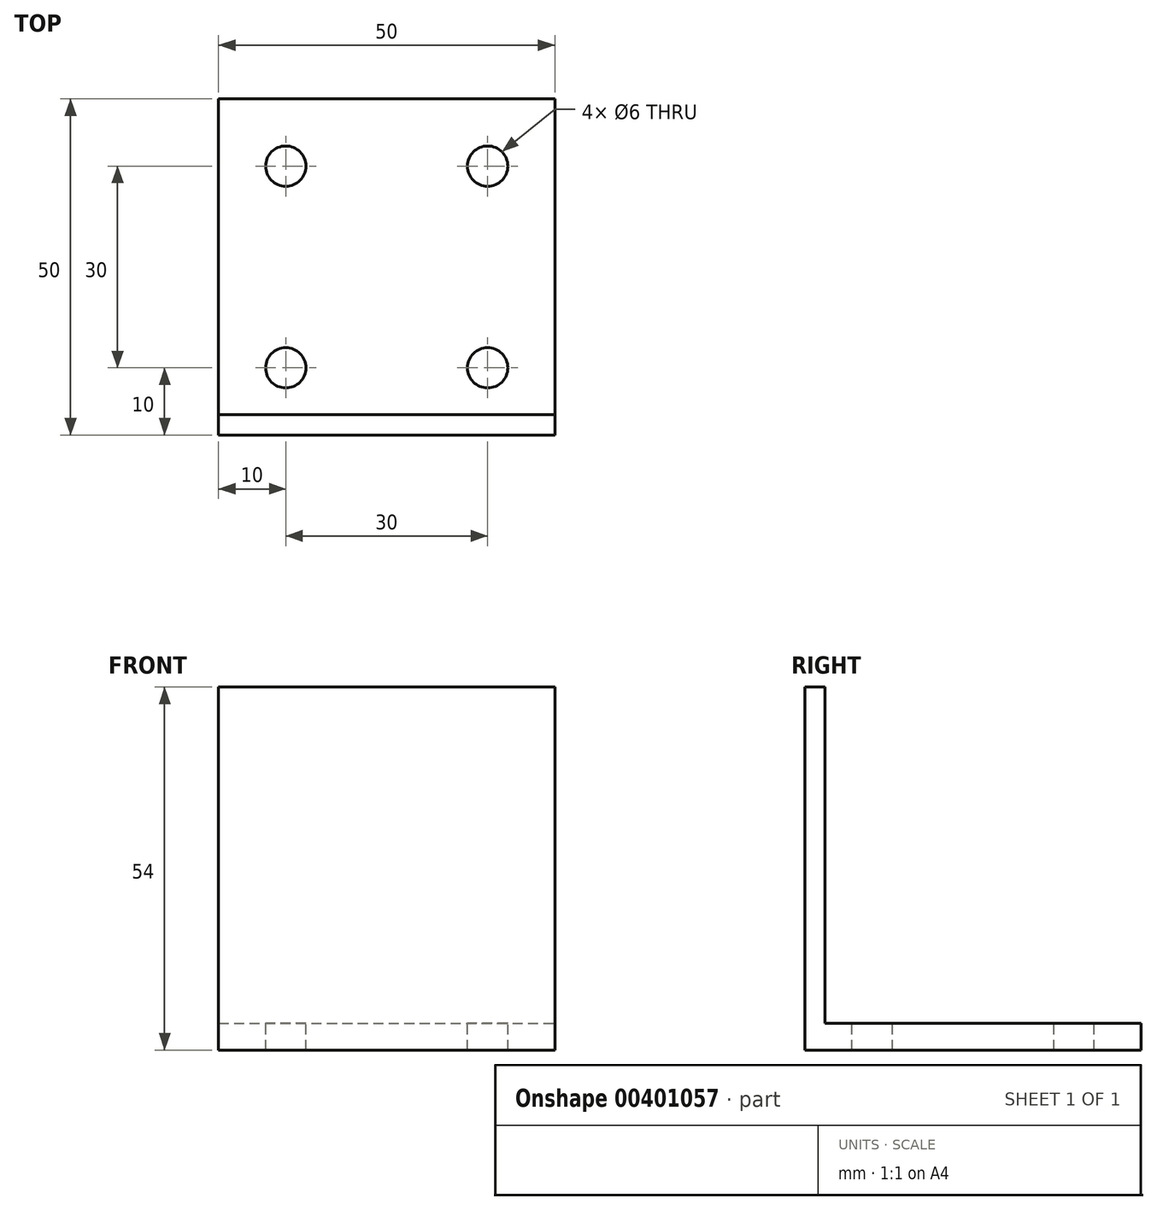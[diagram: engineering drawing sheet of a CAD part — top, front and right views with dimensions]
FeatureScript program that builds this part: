
annotation { "Feature Type Name" : "Feature", "Feature Type Description" : "" }
export const myFeature = defineFeature(function(context is Context, id is Id, definition is map)
    precondition{}
    {
        {
            var Q0;
            Q0=qCreatedBy(makeId("Top.planeOp"),FACE);
            var sketch = newSketch(context, id + "F0", { "sketchPlane" : qUnion([Q0])});
            skLineSegment(sketch, "E0.bottom", {"start": v(-25, 25) * mm, "end": v(25, 25) * mm});
            skLineSegment(sketch, "E0.top", {"start": v(-25, -25) * mm, "end": v(25, -25) * mm});
            skLineSegment(sketch, "E0.left", {"start": v(-25, 25) * mm, "end": v(-25, -25) * mm});
            skLineSegment(sketch, "E0.right", {"start": v(25, 25) * mm, "end": v(25, -25) * mm});
            skSolve(sketch);
        }
        {
            var Q0;
            Q0=makeQuery(id+"F0.imprint","IMPRINT",FACE,{"disambiguationData":[TD([[makeQuery(id+"F0.imprint","IMPRINT",EDGE,{"derivedFrom":sQuery(id+"F0.wireOp",EDGE,"E0.bottom")}),-1.0]])]});
            extrude(context, id + "F1", {"entities" : qUnion([Q0]), "depth" : 4 * mm});
        }
        {
            var Q0;
            Q0=makeQuery(id+"F1.opExtrude","CAP_FACE",FACE,{"disambiguationData":[OSD([sQuery(id+"F0.wireOp",EDGE,"E0.bottom"),sQuery(id+"F0.wireOp",EDGE,"E0.top"),sQuery(id+"F0.wireOp",EDGE,"E0.left"),sQuery(id+"F0.wireOp",EDGE,"E0.right")])],"isStart":false});
            var sketch = newSketch(context, id + "F2", { "sketchPlane" : qUnion([Q0])});
            skLineSegment(sketch, "E1.bottom", {"start": v(-25, -25) * mm, "end": v(25, -25) * mm});
            skLineSegment(sketch, "E1.top", {"start": v(-25, -22) * mm, "end": v(25, -22) * mm});
            skLineSegment(sketch, "E1.left", {"start": v(-25, -25) * mm, "end": v(-25, -22) * mm});
            skLineSegment(sketch, "E1.right", {"start": v(25, -25) * mm, "end": v(25, -22) * mm});
            skSolve(sketch);
        }
        {
            var Q0;
            Q0=makeQuery(id+"F2.imprint","IMPRINT",FACE,{"disambiguationData":[TD([[makeQuery(id+"F2.imprint","IMPRINT",EDGE,{"derivedFrom":sQuery(id+"F2.wireOp",EDGE,"E1.bottom")}),1.0]])]});
            extrude(context, id + "F3", {"entities" : qUnion([Q0]), "operationType" : NewBodyOperationType.ADD, "depth" : 50 * mm});
        }
        {
            var Q0;
            Q0=makeQuery(id+"F1.opExtrude","CAP_FACE",FACE,{"disambiguationData":[OSD([sQuery(id+"F0.wireOp",EDGE,"E0.bottom"),sQuery(id+"F0.wireOp",EDGE,"E0.top"),sQuery(id+"F0.wireOp",EDGE,"E0.left"),sQuery(id+"F0.wireOp",EDGE,"E0.right")])],"isStart":false});
            var sketch = newSketch(context, id + "F4", { "sketchPlane" : qUnion([Q0])});
            skCircle(sketch, "E2", {"center": v(-15, -15) * mm, "radius": 3 * mm});
            skCircle(sketch, "E3.1.0", {"center": v(15, -15) * mm, "radius": 3 * mm});
            skCircle(sketch, "E3.2.0", {"center": v(15, 15) * mm, "radius": 3 * mm});
            skCircle(sketch, "E3.3.0", {"center": v(-15, 15) * mm, "radius": 3 * mm});
            skPoint(sketch, "E3.center", {"position": v(0, 0) * mm});
            skSolve(sketch);
        }
        {
            var Q0;
            Q0=makeQuery(id+"F4.imprint","IMPRINT",FACE,{"disambiguationData":[TD([[makeQuery(id+"F4.imprint","IMPRINT",EDGE,{"derivedFrom":sQuery(id+"F4.wireOp",EDGE,"E3.3.0")}),1.0]])]});
            var Q1;
            Q1=makeQuery(id+"F4.imprint","IMPRINT",FACE,{"disambiguationData":[TD([[makeQuery(id+"F4.imprint","IMPRINT",EDGE,{"derivedFrom":sQuery(id+"F4.wireOp",EDGE,"E2")}),1.0]])]});
            var Q2;
            Q2=makeQuery(id+"F4.imprint","IMPRINT",FACE,{"disambiguationData":[TD([[makeQuery(id+"F4.imprint","IMPRINT",EDGE,{"derivedFrom":sQuery(id+"F4.wireOp",EDGE,"E3.1.0")}),1.0]])]});
            var Q3;
            Q3=makeQuery(id+"F4.imprint","IMPRINT",FACE,{"disambiguationData":[TD([[makeQuery(id+"F4.imprint","IMPRINT",EDGE,{"derivedFrom":sQuery(id+"F4.wireOp",EDGE,"E3.2.0")}),1.0]])]});
            extrude(context, id + "F5", {"entities" : qUnion([Q0, Q1, Q2, Q3]), "operationType" : NewBodyOperationType.REMOVE, "oppositeDirection" : true, "depth" : 25 * mm});
        }
    });
